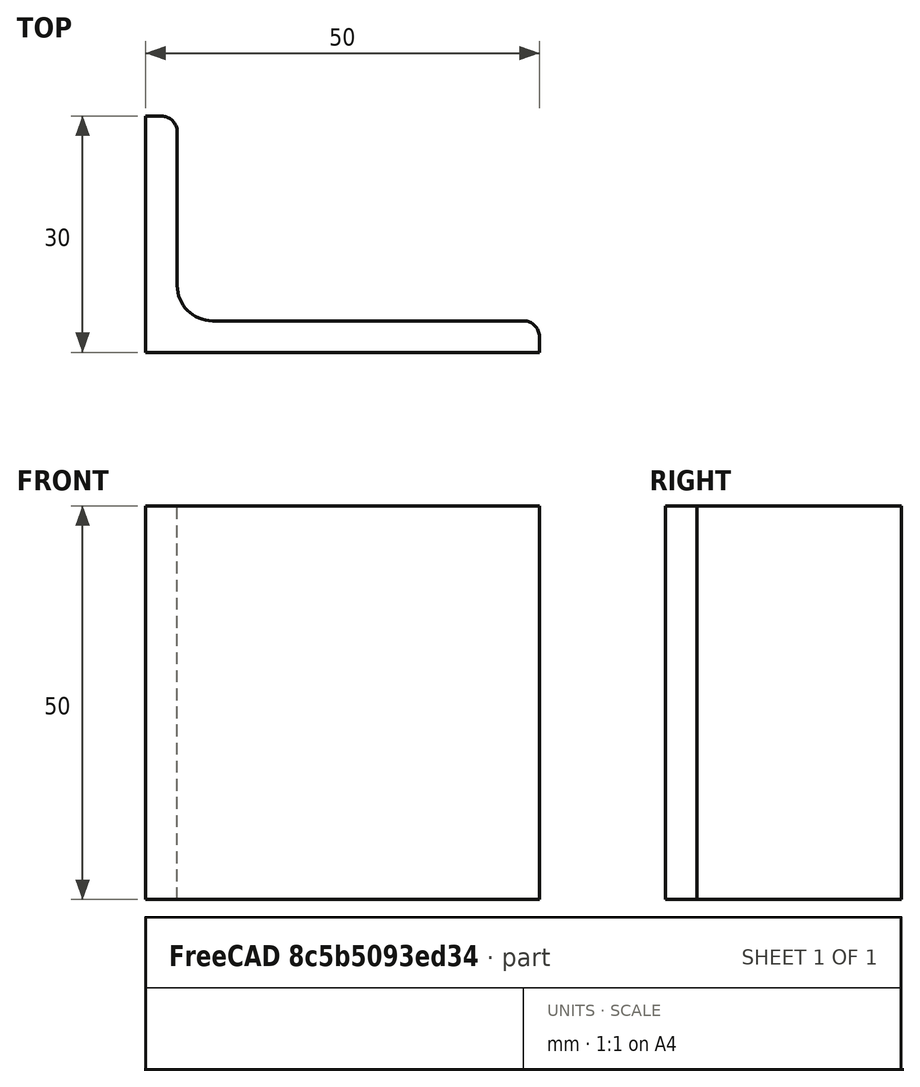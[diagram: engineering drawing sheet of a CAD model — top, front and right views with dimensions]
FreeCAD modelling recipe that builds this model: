
FCSTD DOCUMENT  (FreeCAD 0.15R4671 (Git))
Label: Angle Bar 50x30x4 EN10056 S235JR
License: All rights reserved
LicenseURL: http://en.wikipedia.org/wiki/All_rights_reserved
objects: Sketcher::SketchObject×1, Part::Extrusion×1
note: 2 computed .brp shape members not serialized (recipe doc carries the construction recipe); baked Part::Feature solids carry a one-line shape summary decoded from their .brp

FEATURE [Sketcher::SketchObject] Sketch
  sketch-geometry (9):
    g0: LineSegment StartX=0 StartY=0 StartZ=0 EndX=50 EndY=0 EndZ=0
    g1: LineSegment StartX=50 StartY=0 StartZ=0 EndX=50 EndY=2 EndZ=0
    g2: LineSegment StartX=48 StartY=4 StartZ=0 EndX=8.5 EndY=4 EndZ=0
    g3: LineSegment StartX=0 StartY=0 StartZ=0 EndX=0 EndY=30 EndZ=0
    g4: LineSegment StartX=0 StartY=30 StartZ=0 EndX=2 EndY=30 EndZ=0
    g5: LineSegment StartX=4 StartY=28 StartZ=0 EndX=4 EndY=8.5 EndZ=0
    g6: ArcOfCircle CenterX=8.5 CenterY=8.5 CenterZ=0 NormalX=0 NormalY=0 NormalZ=1 Radius=4.5 StartAngle=3.14159 EndAngle=4.71239
    g7: ArcOfCircle CenterX=2 CenterY=28 CenterZ=0 NormalX=0 NormalY=0 NormalZ=1 Radius=2 StartAngle=0 EndAngle=1.5708
    g8: ArcOfCircle CenterX=48 CenterY=2 CenterZ=0 NormalX=0 NormalY=0 NormalZ=1 Radius=2 StartAngle=0 EndAngle=1.5708
  constraints (23):
    c: Coincident(g0,g-1)
    c: Horizontal(g0)
    c: Coincident(g1,g0)
    c: Vertical(g1)
    c: Horizontal(g2)
    c: Coincident(g3,g-1)
    c: Vertical(g3)
    c: Coincident(g4,g3)
    c: Horizontal(g4)
    c: Vertical(g5)
    c: Tangent(g5,g6) = -1.5708
    c: Tangent(g2,g6) = 1.5708
    c: Tangent(g4,g7) = 1.5708
    c: Tangent(g5,g7) = 1.5708
    c: Tangent(g2,g8) = -1.5708
    c: Tangent(g1,g8) = -1.5708
    c: DistanceX(g0) = 50
    c: DistanceY(g3) = 30
    c: DistanceY(g0,g2) = 4
    c: DistanceX(g3,g5) = 4
    c: Radius(g6) = 4.5
    c: Radius(g8) = 2
    c: Radius(g7) = 2
FEATURE [Part::Extrusion] Extrude  label="Angle Bar 50x30x4 EN10056 S235JR"
  Base = -> Sketch
  Dir = (0,0,50)
  Solid = true
